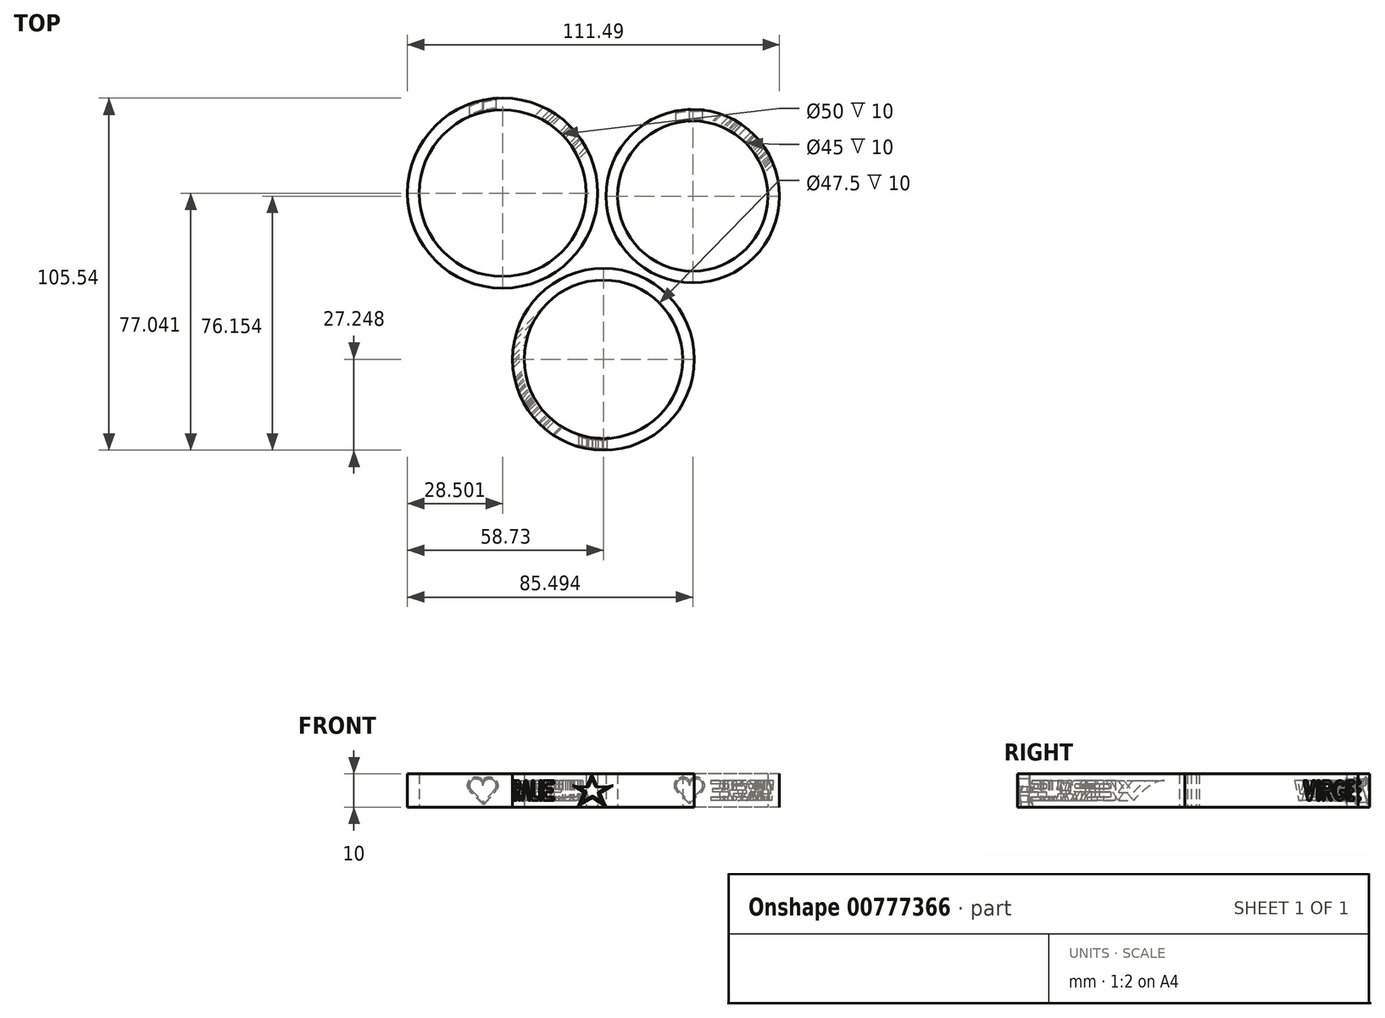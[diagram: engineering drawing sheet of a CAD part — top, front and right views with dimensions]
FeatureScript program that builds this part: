
annotation { "Feature Type Name" : "Feature", "Feature Type Description" : "" }
export const myFeature = defineFeature(function(context is Context, id is Id, definition is map)
    precondition{}
    {
        {
            var Q0;
            Q0=qCreatedBy(makeId("Top.planeOp"),FACE);
            var sketch = newSketch(context, id + "F0", { "sketchPlane" : qUnion([Q0])});
            skCircle(sketch, "E0", {"center": v(-30.23, 32.27) * mm, "radius": 25 * mm});
            skCircle(sketch, "E1", {"center": v(-30.23, 32.27) * mm, "radius": 28.5 * mm});
            skCircle(sketch, "E2", {"center": v(26.76, 31.38) * mm, "radius": 22.5 * mm});
            skCircle(sketch, "E3", {"center": v(26.76, 31.38) * mm, "radius": 26 * mm});
            skCircle(sketch, "E4", {"center": v(0, -17.52) * mm, "radius": 23.75 * mm});
            skCircle(sketch, "E5", {"center": v(0, -17.52) * mm, "radius": 27.25 * mm});
            skSolve(sketch);
        }
        {
            var Q0;
            Q0=makeQuery(id+"F0.imprint","IMPRINT",FACE,{"disambiguationData":[TD([[makeQuery(id+"F0.imprint","IMPRINT",EDGE,{"derivedFrom":sQuery(id+"F0.wireOp",EDGE,"E4")}),-1.0]])]});
            var Q1;
            Q1=makeQuery(id+"F0.imprint","IMPRINT",FACE,{"disambiguationData":[TD([[makeQuery(id+"F0.imprint","IMPRINT",EDGE,{"derivedFrom":sQuery(id+"F0.wireOp",EDGE,"E2")}),-1.0]])]});
            var Q2;
            Q2=makeQuery(id+"F0.imprint","IMPRINT",FACE,{"disambiguationData":[TD([[makeQuery(id+"F0.imprint","IMPRINT",EDGE,{"derivedFrom":sQuery(id+"F0.wireOp",EDGE,"E0")}),-1.0]])]});
            extrude(context, id + "F1", {"entities" : qUnion([Q0, Q1, Q2]), "depth" : 10 * mm, "offsetDistance" : 25 * mm});
        }
        {
            var Q0;
            Q0=qCreatedBy(makeId("Front.planeOp"),FACE);
            cPlane(context, id + "F2", {"entities" : qUnion([Q0]), "cplaneType" : CPlaneType.OFFSET, "offset" : 81.8 * mm, "width" : 150 * mm, "height" : 150 * mm});
        }
        {
            var Q0;
            Q0=qCreatedBy(id+"F2.planeOp",FACE);
            var sketch = newSketch(context, id + "F3", { "sketchPlane" : qUnion([Q0])});
            skLineSegment(sketch, "E6", {"start": v(-3.41, 8.5) * mm, "end": v(-0.41, 1.5) * mm});
            skLineSegment(sketch, "E7", {"start": v(-0.41, 1.5) * mm, "end": v(-7.41, 6) * mm});
            skLineSegment(sketch, "E8", {"start": v(-7.41, 6) * mm, "end": v(1.09, 6) * mm});
            skLineSegment(sketch, "E9", {"start": v(1.09, 6) * mm, "end": v(-6.41, 1.5) * mm});
            skLineSegment(sketch, "E10", {"start": v(-6.41, 1.5) * mm, "end": v(-3.41, 8.5) * mm});
            skSolve(sketch);
        }
        {
            var Q0;
            {var subQ0=sQuery(id+"F3.wireOp",EDGE,"E10");var subQ1=sQuery(id+"F3.wireOp",EDGE,"E6");var subQ2=makeQuery(id+"F3.imprint","INTERSECT",VERTEX,{"derivedFrom":[subQ1,subQ0]});Q0=makeQuery(id+"F3.imprint","IMPRINT",FACE,{"disambiguationData":[TD([[makeQuery(id+"F3.imprint","IMPRINT",EDGE,{"disambiguationData":[TD([[subQ2,-1.0]])],"derivedFrom":subQ1}),-1.0]])]});}
            var Q1;
            {var subQ0=sQuery(id+"F3.wireOp",EDGE,"E7");var subQ1=sQuery(id+"F3.wireOp",EDGE,"E6");var subQ2=makeQuery(id+"F3.imprint","INTERSECT",VERTEX,{"derivedFrom":[subQ1,subQ0]});Q1=makeQuery(id+"F3.imprint","IMPRINT",FACE,{"disambiguationData":[TD([[makeQuery(id+"F3.imprint","IMPRINT",EDGE,{"disambiguationData":[TD([[subQ2,1.0]])],"derivedFrom":subQ1}),-1.0]])]});}
            var Q2;
            {var subQ0=sQuery(id+"F3.wireOp",EDGE,"E9");var subQ1=sQuery(id+"F3.wireOp",EDGE,"E7");var subQ2=makeQuery(id+"F3.imprint","INTERSECT",VERTEX,{"derivedFrom":[subQ1,subQ0]});Q2=makeQuery(id+"F3.imprint","IMPRINT",FACE,{"disambiguationData":[TD([[makeQuery(id+"F3.imprint","IMPRINT",EDGE,{"disambiguationData":[TD([[subQ2,-1.0]])],"derivedFrom":subQ1}),1.0]])]});}
            var Q3;
            {var subQ1=sQuery(id+"F3.wireOp",EDGE,"E6");var subQ5=sQuery(id+"F3.wireOp",EDGE,"E8");var subQ6=makeQuery(id+"F3.imprint","INTERSECT",VERTEX,{"derivedFrom":[subQ1,subQ5]});Q3=makeQuery(id+"F3.imprint","IMPRINT",FACE,{"disambiguationData":[TD([[makeQuery(id+"F3.imprint","IMPRINT",EDGE,{"disambiguationData":[TD([[subQ6,-1.0]])],"derivedFrom":subQ1}),-1.0]])]});}
            var Q4;
            {var subQ0=sQuery(id+"F3.wireOp",EDGE,"E8");var subQ1=sQuery(id+"F3.wireOp",EDGE,"E6");var subQ2=makeQuery(id+"F3.imprint","INTERSECT",VERTEX,{"derivedFrom":[subQ1,subQ0]});Q4=makeQuery(id+"F3.imprint","IMPRINT",FACE,{"disambiguationData":[TD([[makeQuery(id+"F3.imprint","IMPRINT",EDGE,{"disambiguationData":[TD([[subQ2,-1.0]])],"derivedFrom":subQ1}),1.0]])]});}
            var Q5;
            {var subQ0=sQuery(id+"F3.wireOp",EDGE,"E8");var subQ1=sQuery(id+"F3.wireOp",EDGE,"E7");var subQ2=makeQuery(id+"F3.imprint","INTERSECT",VERTEX,{"derivedFrom":[subQ1,subQ0]});Q5=makeQuery(id+"F3.imprint","IMPRINT",FACE,{"disambiguationData":[TD([[makeQuery(id+"F3.imprint","IMPRINT",EDGE,{"disambiguationData":[TD([[subQ2,1.0]])],"derivedFrom":subQ1}),-1.0]])]});}
            extrude(context, id + "F4", {"entities" : qUnion([Q0, Q1, Q2, Q3, Q4, Q5]), "operationType" : NewBodyOperationType.REMOVE, "oppositeDirection" : true, "depth" : 58.8 * mm, "offsetDistance" : 25 * mm});
        }
        {
            var Q0;
            {var subQ0=sQuery(id+"F3.wireOp",EDGE,"E7");Q0=makeQuery(id+"F4.boolean.opBoolean","INTERSECT",EDGE,{"derivedFrom":[makeQuery(id+"F1.opExtrude","SWEPT_FACE",FACE,{"disambiguationData":[OSD([sQuery(id+"F0.wireOp",EDGE,"E4")])]}),makeQuery(id+"F4.opExtrude","SWEPT_FACE",FACE,{"disambiguationData":[OSD([subQ0]),TDD([makeQuery(id+"F3.imprint","IMPRINT",EDGE,{"disambiguationData":[TD([[makeQuery(id+"F3.imprint","INTERSECT",VERTEX,{"derivedFrom":[sQuery(id+"F3.wireOp",EDGE,"E6"),subQ0]}),-1.0]])],"derivedFrom":subQ0})])]})]});}
            var Q1;
            {var subQ0=sQuery(id+"F3.wireOp",EDGE,"E6");Q1=makeQuery(id+"F4.boolean.opBoolean","INTERSECT",EDGE,{"derivedFrom":[makeQuery(id+"F1.opExtrude","SWEPT_FACE",FACE,{"disambiguationData":[OSD([sQuery(id+"F0.wireOp",EDGE,"E4")])]}),makeQuery(id+"F4.opExtrude","SWEPT_FACE",FACE,{"disambiguationData":[OSD([subQ0]),TDD([makeQuery(id+"F3.imprint","IMPRINT",EDGE,{"disambiguationData":[TD([[makeQuery(id+"F3.imprint","INTERSECT",VERTEX,{"derivedFrom":[subQ0,sQuery(id+"F3.wireOp",EDGE,"E7")]}),1.0]])],"derivedFrom":subQ0})])]})]});}
            var Q2;
            {var subQ0=sQuery(id+"F3.wireOp",EDGE,"E9");Q2=makeQuery(id+"F4.boolean.opBoolean","INTERSECT",EDGE,{"derivedFrom":[makeQuery(id+"F1.opExtrude","SWEPT_FACE",FACE,{"disambiguationData":[OSD([sQuery(id+"F0.wireOp",EDGE,"E4")])]}),makeQuery(id+"F4.opExtrude","SWEPT_FACE",FACE,{"disambiguationData":[OSD([subQ0]),TDD([makeQuery(id+"F3.imprint","IMPRINT",EDGE,{"disambiguationData":[TD([[makeQuery(id+"F3.imprint","INTERSECT",VERTEX,{"derivedFrom":[sQuery(id+"F3.wireOp",EDGE,"E8"),subQ0]}),-1.0]])],"derivedFrom":subQ0})])]})]});}
            var Q3;
            {var subQ0=sQuery(id+"F3.wireOp",EDGE,"E8");Q3=makeQuery(id+"F4.boolean.opBoolean","INTERSECT",EDGE,{"derivedFrom":[makeQuery(id+"F1.opExtrude","SWEPT_FACE",FACE,{"disambiguationData":[OSD([sQuery(id+"F0.wireOp",EDGE,"E4")])]}),makeQuery(id+"F4.opExtrude","SWEPT_FACE",FACE,{"disambiguationData":[OSD([subQ0]),TDD([makeQuery(id+"F3.imprint","IMPRINT",EDGE,{"disambiguationData":[TD([[makeQuery(id+"F3.imprint","INTERSECT",VERTEX,{"derivedFrom":[subQ0,sQuery(id+"F3.wireOp",EDGE,"E9")]}),1.0]])],"derivedFrom":subQ0})])]})]});}
            var Q4;
            {var subQ0=sQuery(id+"F3.wireOp",EDGE,"E6");Q4=makeQuery(id+"F4.boolean.opBoolean","INTERSECT",EDGE,{"derivedFrom":[makeQuery(id+"F1.opExtrude","SWEPT_FACE",FACE,{"disambiguationData":[OSD([sQuery(id+"F0.wireOp",EDGE,"E4")])]}),makeQuery(id+"F4.opExtrude","SWEPT_FACE",FACE,{"disambiguationData":[OSD([subQ0]),TDD([makeQuery(id+"F3.imprint","IMPRINT",EDGE,{"disambiguationData":[TD([[makeQuery(id+"F3.imprint","INTERSECT",VERTEX,{"derivedFrom":[subQ0,sQuery(id+"F3.wireOp",EDGE,"E10")]}),-1.0]])],"derivedFrom":subQ0})])]})]});}
            var Q5;
            {var subQ0=sQuery(id+"F3.wireOp",EDGE,"E10");Q5=makeQuery(id+"F4.boolean.opBoolean","INTERSECT",EDGE,{"derivedFrom":[makeQuery(id+"F1.opExtrude","SWEPT_FACE",FACE,{"disambiguationData":[OSD([sQuery(id+"F0.wireOp",EDGE,"E4")])]}),makeQuery(id+"F4.opExtrude","SWEPT_FACE",FACE,{"disambiguationData":[OSD([subQ0]),TDD([makeQuery(id+"F3.imprint","IMPRINT",EDGE,{"disambiguationData":[TD([[makeQuery(id+"F3.imprint","INTERSECT",VERTEX,{"derivedFrom":[sQuery(id+"F3.wireOp",EDGE,"E6"),subQ0]}),1.0]])],"derivedFrom":subQ0})])]})]});}
            var Q6;
            {var subQ0=sQuery(id+"F3.wireOp",EDGE,"E8");Q6=makeQuery(id+"F4.boolean.opBoolean","INTERSECT",EDGE,{"derivedFrom":[makeQuery(id+"F1.opExtrude","SWEPT_FACE",FACE,{"disambiguationData":[OSD([sQuery(id+"F0.wireOp",EDGE,"E4")])]}),makeQuery(id+"F4.opExtrude","SWEPT_FACE",FACE,{"disambiguationData":[OSD([subQ0]),TDD([makeQuery(id+"F3.imprint","IMPRINT",EDGE,{"disambiguationData":[TD([[makeQuery(id+"F3.imprint","INTERSECT",VERTEX,{"derivedFrom":[sQuery(id+"F3.wireOp",EDGE,"E7"),subQ0]}),-1.0]])],"derivedFrom":subQ0})])]})]});}
            var Q7;
            {var subQ0=sQuery(id+"F3.wireOp",EDGE,"E7");Q7=makeQuery(id+"F4.boolean.opBoolean","INTERSECT",EDGE,{"derivedFrom":[makeQuery(id+"F1.opExtrude","SWEPT_FACE",FACE,{"disambiguationData":[OSD([sQuery(id+"F0.wireOp",EDGE,"E4")])]}),makeQuery(id+"F4.opExtrude","SWEPT_FACE",FACE,{"disambiguationData":[OSD([subQ0]),TDD([makeQuery(id+"F3.imprint","IMPRINT",EDGE,{"disambiguationData":[TD([[makeQuery(id+"F3.imprint","INTERSECT",VERTEX,{"derivedFrom":[subQ0,sQuery(id+"F3.wireOp",EDGE,"E8")]}),1.0]])],"derivedFrom":subQ0})])]})]});}
            var Q8;
            {var subQ0=sQuery(id+"F3.wireOp",EDGE,"E10");Q8=makeQuery(id+"F4.boolean.opBoolean","INTERSECT",EDGE,{"derivedFrom":[makeQuery(id+"F1.opExtrude","SWEPT_FACE",FACE,{"disambiguationData":[OSD([sQuery(id+"F0.wireOp",EDGE,"E4")])]}),makeQuery(id+"F4.opExtrude","SWEPT_FACE",FACE,{"disambiguationData":[OSD([subQ0]),TDD([makeQuery(id+"F3.imprint","IMPRINT",EDGE,{"disambiguationData":[TD([[makeQuery(id+"F3.imprint","INTERSECT",VERTEX,{"derivedFrom":[sQuery(id+"F3.wireOp",EDGE,"E9"),subQ0]}),-1.0]])],"derivedFrom":subQ0})])]})]});}
            var Q9;
            {var subQ0=sQuery(id+"F3.wireOp",EDGE,"E9");Q9=makeQuery(id+"F4.boolean.opBoolean","INTERSECT",EDGE,{"derivedFrom":[makeQuery(id+"F1.opExtrude","SWEPT_FACE",FACE,{"disambiguationData":[OSD([sQuery(id+"F0.wireOp",EDGE,"E4")])]}),makeQuery(id+"F4.opExtrude","SWEPT_FACE",FACE,{"disambiguationData":[OSD([subQ0]),TDD([makeQuery(id+"F3.imprint","IMPRINT",EDGE,{"disambiguationData":[TD([[makeQuery(id+"F3.imprint","INTERSECT",VERTEX,{"derivedFrom":[subQ0,sQuery(id+"F3.wireOp",EDGE,"E10")]}),1.0]])],"derivedFrom":subQ0})])]})]});}
            fillet(context, id + "F5", {"entities" : qUnion([Q0, Q1, Q2, Q3, Q4, Q5, Q6, Q7, Q8, Q9]), "radius" : .5 * mm, "tangentPropagation" : true, "allowEdgeOverflow" : false});
        }
        {
            var Q0;
            {var subQ0=sQuery(id+"F3.wireOp",EDGE,"E7");Q0=makeQuery(id+"F4.boolean.opBoolean","INTERSECT",EDGE,{"derivedFrom":[makeQuery(id+"F1.opExtrude","SWEPT_FACE",FACE,{"disambiguationData":[OSD([sQuery(id+"F0.wireOp",EDGE,"E5")])]}),makeQuery(id+"F4.opExtrude","SWEPT_FACE",FACE,{"disambiguationData":[OSD([subQ0]),TDD([makeQuery(id+"F3.imprint","IMPRINT",EDGE,{"disambiguationData":[TD([[makeQuery(id+"F3.imprint","INTERSECT",VERTEX,{"derivedFrom":[sQuery(id+"F3.wireOp",EDGE,"E6"),subQ0]}),-1.0]])],"derivedFrom":subQ0})])]})]});}
            var Q1;
            {var subQ0=sQuery(id+"F3.wireOp",EDGE,"E9");Q1=makeQuery(id+"F4.boolean.opBoolean","INTERSECT",EDGE,{"derivedFrom":[makeQuery(id+"F1.opExtrude","SWEPT_FACE",FACE,{"disambiguationData":[OSD([sQuery(id+"F0.wireOp",EDGE,"E5")])]}),makeQuery(id+"F4.opExtrude","SWEPT_FACE",FACE,{"disambiguationData":[OSD([subQ0]),TDD([makeQuery(id+"F3.imprint","IMPRINT",EDGE,{"disambiguationData":[TD([[makeQuery(id+"F3.imprint","INTERSECT",VERTEX,{"derivedFrom":[subQ0,sQuery(id+"F3.wireOp",EDGE,"E10")]}),1.0]])],"derivedFrom":subQ0})])]})]});}
            var Q2;
            {var subQ0=sQuery(id+"F3.wireOp",EDGE,"E10");Q2=makeQuery(id+"F4.boolean.opBoolean","INTERSECT",EDGE,{"derivedFrom":[makeQuery(id+"F1.opExtrude","SWEPT_FACE",FACE,{"disambiguationData":[OSD([sQuery(id+"F0.wireOp",EDGE,"E5")])]}),makeQuery(id+"F4.opExtrude","SWEPT_FACE",FACE,{"disambiguationData":[OSD([subQ0]),TDD([makeQuery(id+"F3.imprint","IMPRINT",EDGE,{"disambiguationData":[TD([[makeQuery(id+"F3.imprint","INTERSECT",VERTEX,{"derivedFrom":[sQuery(id+"F3.wireOp",EDGE,"E9"),subQ0]}),-1.0]])],"derivedFrom":subQ0})])]})]});}
            var Q3;
            {var subQ0=sQuery(id+"F3.wireOp",EDGE,"E7");Q3=makeQuery(id+"F4.boolean.opBoolean","INTERSECT",EDGE,{"derivedFrom":[makeQuery(id+"F1.opExtrude","SWEPT_FACE",FACE,{"disambiguationData":[OSD([sQuery(id+"F0.wireOp",EDGE,"E5")])]}),makeQuery(id+"F4.opExtrude","SWEPT_FACE",FACE,{"disambiguationData":[OSD([subQ0]),TDD([makeQuery(id+"F3.imprint","IMPRINT",EDGE,{"disambiguationData":[TD([[makeQuery(id+"F3.imprint","INTERSECT",VERTEX,{"derivedFrom":[subQ0,sQuery(id+"F3.wireOp",EDGE,"E8")]}),1.0]])],"derivedFrom":subQ0})])]})]});}
            var Q4;
            {var subQ0=sQuery(id+"F3.wireOp",EDGE,"E8");Q4=makeQuery(id+"F4.boolean.opBoolean","INTERSECT",EDGE,{"derivedFrom":[makeQuery(id+"F1.opExtrude","SWEPT_FACE",FACE,{"disambiguationData":[OSD([sQuery(id+"F0.wireOp",EDGE,"E5")])]}),makeQuery(id+"F4.opExtrude","SWEPT_FACE",FACE,{"disambiguationData":[OSD([subQ0]),TDD([makeQuery(id+"F3.imprint","IMPRINT",EDGE,{"disambiguationData":[TD([[makeQuery(id+"F3.imprint","INTERSECT",VERTEX,{"derivedFrom":[sQuery(id+"F3.wireOp",EDGE,"E7"),subQ0]}),-1.0]])],"derivedFrom":subQ0})])]})]});}
            var Q5;
            {var subQ0=sQuery(id+"F3.wireOp",EDGE,"E10");Q5=makeQuery(id+"F4.boolean.opBoolean","INTERSECT",EDGE,{"derivedFrom":[makeQuery(id+"F1.opExtrude","SWEPT_FACE",FACE,{"disambiguationData":[OSD([sQuery(id+"F0.wireOp",EDGE,"E5")])]}),makeQuery(id+"F4.opExtrude","SWEPT_FACE",FACE,{"disambiguationData":[OSD([subQ0]),TDD([makeQuery(id+"F3.imprint","IMPRINT",EDGE,{"disambiguationData":[TD([[makeQuery(id+"F3.imprint","INTERSECT",VERTEX,{"derivedFrom":[sQuery(id+"F3.wireOp",EDGE,"E6"),subQ0]}),1.0]])],"derivedFrom":subQ0})])]})]});}
            var Q6;
            {var subQ0=sQuery(id+"F3.wireOp",EDGE,"E6");Q6=makeQuery(id+"F4.boolean.opBoolean","INTERSECT",EDGE,{"derivedFrom":[makeQuery(id+"F1.opExtrude","SWEPT_FACE",FACE,{"disambiguationData":[OSD([sQuery(id+"F0.wireOp",EDGE,"E5")])]}),makeQuery(id+"F4.opExtrude","SWEPT_FACE",FACE,{"disambiguationData":[OSD([subQ0]),TDD([makeQuery(id+"F3.imprint","IMPRINT",EDGE,{"disambiguationData":[TD([[makeQuery(id+"F3.imprint","INTERSECT",VERTEX,{"derivedFrom":[subQ0,sQuery(id+"F3.wireOp",EDGE,"E10")]}),-1.0]])],"derivedFrom":subQ0})])]})]});}
            var Q7;
            {var subQ0=sQuery(id+"F3.wireOp",EDGE,"E8");Q7=makeQuery(id+"F4.boolean.opBoolean","INTERSECT",EDGE,{"derivedFrom":[makeQuery(id+"F1.opExtrude","SWEPT_FACE",FACE,{"disambiguationData":[OSD([sQuery(id+"F0.wireOp",EDGE,"E5")])]}),makeQuery(id+"F4.opExtrude","SWEPT_FACE",FACE,{"disambiguationData":[OSD([subQ0]),TDD([makeQuery(id+"F3.imprint","IMPRINT",EDGE,{"disambiguationData":[TD([[makeQuery(id+"F3.imprint","INTERSECT",VERTEX,{"derivedFrom":[subQ0,sQuery(id+"F3.wireOp",EDGE,"E9")]}),1.0]])],"derivedFrom":subQ0})])]})]});}
            var Q8;
            {var subQ0=sQuery(id+"F3.wireOp",EDGE,"E9");Q8=makeQuery(id+"F4.boolean.opBoolean","INTERSECT",EDGE,{"derivedFrom":[makeQuery(id+"F1.opExtrude","SWEPT_FACE",FACE,{"disambiguationData":[OSD([sQuery(id+"F0.wireOp",EDGE,"E5")])]}),makeQuery(id+"F4.opExtrude","SWEPT_FACE",FACE,{"disambiguationData":[OSD([subQ0]),TDD([makeQuery(id+"F3.imprint","IMPRINT",EDGE,{"disambiguationData":[TD([[makeQuery(id+"F3.imprint","INTERSECT",VERTEX,{"derivedFrom":[sQuery(id+"F3.wireOp",EDGE,"E8"),subQ0]}),-1.0]])],"derivedFrom":subQ0})])]})]});}
            var Q9;
            {var subQ0=sQuery(id+"F3.wireOp",EDGE,"E6");Q9=makeQuery(id+"F4.boolean.opBoolean","INTERSECT",EDGE,{"derivedFrom":[makeQuery(id+"F1.opExtrude","SWEPT_FACE",FACE,{"disambiguationData":[OSD([sQuery(id+"F0.wireOp",EDGE,"E5")])]}),makeQuery(id+"F4.opExtrude","SWEPT_FACE",FACE,{"disambiguationData":[OSD([subQ0]),TDD([makeQuery(id+"F3.imprint","IMPRINT",EDGE,{"disambiguationData":[TD([[makeQuery(id+"F3.imprint","INTERSECT",VERTEX,{"derivedFrom":[subQ0,sQuery(id+"F3.wireOp",EDGE,"E7")]}),1.0]])],"derivedFrom":subQ0})])]})]});}
            fillet(context, id + "F6", {"entities" : qUnion([Q0, Q1, Q2, Q3, Q4, Q5, Q6, Q7, Q8, Q9]), "radius" : .5 * mm, "tangentPropagation" : true, "allowEdgeOverflow" : false});
        }
        {
            var Q0;
            Q0=qCreatedBy(makeId("Front.planeOp"),FACE);
            cPlane(context, id + "F7", {"entities" : qUnion([Q0]), "cplaneType" : CPlaneType.OFFSET, "offset" : 109.91 * mm, "oppositeDirection" : true, "width" : 150 * mm, "height" : 150 * mm});
        }
        {
            var Q0;
            Q0=qCreatedBy(id+"F7.planeOp",FACE);
            var sketch = newSketch(context, id + "F8", { "sketchPlane" : qUnion([Q0])});
            skArc(sketch, "E11", {"start": v(-32.64, 5.17) * mm, "mid": v(-33.43, 8.37) * mm, "end": v(-36.14, 6.5) * mm});
            skArc(sketch, "E12", {"start": v(-36.14, 6.5) * mm, "mid": v(-38.91, 8.34) * mm, "end": v(-39.54, 5.07) * mm});
            skLineSegment(sketch, "E13", {"start": v(-35.9, 1.5) * mm, "end": v(-39.54, 5.07) * mm});
            skLineSegment(sketch, "E14", {"start": v(-39.54, 5.07) * mm, "end": v(-35.9, 1.5) * mm});
            skLineSegment(sketch, "E15", {"start": v(-35.9, 1.5) * mm, "end": v(-32.64, 5.17) * mm});
            skPoint(sketch, "E16.orphan", {"position": v(-35.9, -6.56) * mm});
            skSolve(sketch);
        }
        {
            var Q0;
            Q0 = qSketchRegion(id + "F8", true);
            extrude(context, id + "F9", {"entities" : qUnion([Q0]), "operationType" : NewBodyOperationType.REMOVE, "depth" : 65 * mm, "offsetDistance" : 25 * mm});
        }
        {
            var Q0;
            Q0=makeQuery(id+"F9.boolean.opBoolean","INTERSECT",EDGE,{"derivedFrom":[makeQuery(id+"F1.opExtrude","SWEPT_FACE",FACE,{"disambiguationData":[OSD([sQuery(id+"F0.wireOp",EDGE,"E0")])]}),makeQuery(id+"F9.opExtrude","SWEPT_FACE",FACE,{"disambiguationData":[OSD([sQuery(id+"F8.wireOp",EDGE,"E15")])]})]});
            var Q1;
            Q1=makeQuery(id+"F9.boolean.opBoolean","INTERSECT",EDGE,{"derivedFrom":[makeQuery(id+"F1.opExtrude","SWEPT_FACE",FACE,{"disambiguationData":[OSD([sQuery(id+"F0.wireOp",EDGE,"E0")])]}),makeQuery(id+"F9.opExtrude","SWEPT_FACE",FACE,{"disambiguationData":[OSD([sQuery(id+"F8.wireOp",EDGE,"E14")])]})]});
            var Q2;
            Q2=makeQuery(id+"F9.boolean.opBoolean","INTERSECT",EDGE,{"derivedFrom":[makeQuery(id+"F1.opExtrude","SWEPT_FACE",FACE,{"disambiguationData":[OSD([sQuery(id+"F0.wireOp",EDGE,"E0")])]}),makeQuery(id+"F9.opExtrude","SWEPT_FACE",FACE,{"disambiguationData":[OSD([sQuery(id+"F8.wireOp",EDGE,"E12")])]})]});
            var Q3;
            Q3=makeQuery(id+"F9.boolean.opBoolean","INTERSECT",EDGE,{"derivedFrom":[makeQuery(id+"F1.opExtrude","SWEPT_FACE",FACE,{"disambiguationData":[OSD([sQuery(id+"F0.wireOp",EDGE,"E0")])]}),makeQuery(id+"F9.opExtrude","SWEPT_FACE",FACE,{"disambiguationData":[OSD([sQuery(id+"F8.wireOp",EDGE,"E11")])]})]});
            fillet(context, id + "F10", {"entities" : qUnion([Q0, Q1, Q2, Q3]), "radius" : .5 * mm, "tangentPropagation" : true, "allowEdgeOverflow" : false});
        }
        {
            var Q0;
            Q0=makeQuery(id+"F9.boolean.opBoolean","INTERSECT",EDGE,{"derivedFrom":[makeQuery(id+"F1.opExtrude","SWEPT_FACE",FACE,{"disambiguationData":[OSD([sQuery(id+"F0.wireOp",EDGE,"E1")])]}),makeQuery(id+"F9.opExtrude","SWEPT_FACE",FACE,{"disambiguationData":[OSD([sQuery(id+"F8.wireOp",EDGE,"E14")])]})]});
            var Q1;
            Q1=makeQuery(id+"F9.boolean.opBoolean","INTERSECT",EDGE,{"derivedFrom":[makeQuery(id+"F1.opExtrude","SWEPT_FACE",FACE,{"disambiguationData":[OSD([sQuery(id+"F0.wireOp",EDGE,"E1")])]}),makeQuery(id+"F9.opExtrude","SWEPT_FACE",FACE,{"disambiguationData":[OSD([sQuery(id+"F8.wireOp",EDGE,"E15")])]})]});
            var Q2;
            Q2=makeQuery(id+"F9.boolean.opBoolean","INTERSECT",EDGE,{"derivedFrom":[makeQuery(id+"F1.opExtrude","SWEPT_FACE",FACE,{"disambiguationData":[OSD([sQuery(id+"F0.wireOp",EDGE,"E1")])]}),makeQuery(id+"F9.opExtrude","SWEPT_FACE",FACE,{"disambiguationData":[OSD([sQuery(id+"F8.wireOp",EDGE,"E12")])]})]});
            var Q3;
            Q3=makeQuery(id+"F9.boolean.opBoolean","INTERSECT",EDGE,{"derivedFrom":[makeQuery(id+"F1.opExtrude","SWEPT_FACE",FACE,{"disambiguationData":[OSD([sQuery(id+"F0.wireOp",EDGE,"E1")])]}),makeQuery(id+"F9.opExtrude","SWEPT_FACE",FACE,{"disambiguationData":[OSD([sQuery(id+"F8.wireOp",EDGE,"E11")])]})]});
            fillet(context, id + "F11", {"entities" : qUnion([Q0, Q1, Q2, Q3]), "radius" : .5 * mm, "tangentPropagation" : true, "allowEdgeOverflow" : false});
        }
        {
            var Q0;
            Q0=qCreatedBy(id+"F7.planeOp",FACE);
            var sketch = newSketch(context, id + "F12", { "sketchPlane" : qUnion([Q0])});
            skArc(sketch, "E17", {"start": v(29.18, 5.07) * mm, "mid": v(28.55, 8.34) * mm, "end": v(25.78, 6.5) * mm});
            skArc(sketch, "E18", {"start": v(25.78, 6.5) * mm, "mid": v(23, 8.34) * mm, "end": v(22.38, 5.07) * mm});
            skLineSegment(sketch, "E19", {"start": v(25.78, 1.74) * mm, "end": v(22.38, 5.07) * mm});
            skLineSegment(sketch, "E20", {"start": v(22.38, 5.07) * mm, "end": v(25.78, 1.74) * mm});
            skLineSegment(sketch, "E21", {"start": v(25.78, 1.74) * mm, "end": v(29.18, 5.07) * mm});
            skPoint(sketch, "E22.orphan", {"position": v(25.78, -4.26) * mm});
            skSolve(sketch);
        }
        {
            var Q0;
            Q0=makeQuery(id+"F12.imprint","IMPRINT",FACE,{"disambiguationData":[TD([[makeQuery(id+"F12.imprint","IMPRINT",EDGE,{"derivedFrom":sQuery(id+"F12.wireOp",EDGE,"E17")}),1.0]])]});
            extrude(context, id + "F13", {"entities" : qUnion([Q0]), "operationType" : NewBodyOperationType.REMOVE, "depth" : 92.4 * mm, "offsetDistance" : 25 * mm});
        }
        {
            var Q0;
            Q0=makeQuery(id+"F13.boolean.opBoolean","INTERSECT",EDGE,{"derivedFrom":[makeQuery(id+"F1.opExtrude","SWEPT_FACE",FACE,{"disambiguationData":[OSD([sQuery(id+"F0.wireOp",EDGE,"E2")])]}),makeQuery(id+"F13.opExtrude","SWEPT_FACE",FACE,{"disambiguationData":[OSD([sQuery(id+"F12.wireOp",EDGE,"E21")])]})]});
            var Q1;
            Q1=makeQuery(id+"F13.boolean.opBoolean","INTERSECT",EDGE,{"derivedFrom":[makeQuery(id+"F1.opExtrude","SWEPT_FACE",FACE,{"disambiguationData":[OSD([sQuery(id+"F0.wireOp",EDGE,"E2")])]}),makeQuery(id+"F13.opExtrude","SWEPT_FACE",FACE,{"disambiguationData":[OSD([sQuery(id+"F12.wireOp",EDGE,"E17")])]})]});
            var Q2;
            Q2=makeQuery(id+"F13.boolean.opBoolean","INTERSECT",EDGE,{"derivedFrom":[makeQuery(id+"F1.opExtrude","SWEPT_FACE",FACE,{"disambiguationData":[OSD([sQuery(id+"F0.wireOp",EDGE,"E2")])]}),makeQuery(id+"F13.opExtrude","SWEPT_FACE",FACE,{"disambiguationData":[OSD([sQuery(id+"F12.wireOp",EDGE,"E20")])]})]});
            var Q3;
            Q3=makeQuery(id+"F13.boolean.opBoolean","INTERSECT",EDGE,{"derivedFrom":[makeQuery(id+"F1.opExtrude","SWEPT_FACE",FACE,{"disambiguationData":[OSD([sQuery(id+"F0.wireOp",EDGE,"E2")])]}),makeQuery(id+"F13.opExtrude","SWEPT_FACE",FACE,{"disambiguationData":[OSD([sQuery(id+"F12.wireOp",EDGE,"E18")])]})]});
            fillet(context, id + "F14", {"entities" : qUnion([Q0, Q1, Q2, Q3]), "radius" : .5 * mm, "tangentPropagation" : true, "allowEdgeOverflow" : false});
        }
        {
            var Q0;
            Q0=makeQuery(id+"F13.boolean.opBoolean","INTERSECT",EDGE,{"derivedFrom":[makeQuery(id+"F1.opExtrude","SWEPT_FACE",FACE,{"disambiguationData":[OSD([sQuery(id+"F0.wireOp",EDGE,"E3")])]}),makeQuery(id+"F13.opExtrude","SWEPT_FACE",FACE,{"disambiguationData":[OSD([sQuery(id+"F12.wireOp",EDGE,"E20")])]})]});
            var Q1;
            Q1=makeQuery(id+"F13.boolean.opBoolean","INTERSECT",EDGE,{"derivedFrom":[makeQuery(id+"F1.opExtrude","SWEPT_FACE",FACE,{"disambiguationData":[OSD([sQuery(id+"F0.wireOp",EDGE,"E3")])]}),makeQuery(id+"F13.opExtrude","SWEPT_FACE",FACE,{"disambiguationData":[OSD([sQuery(id+"F12.wireOp",EDGE,"E18")])]})]});
            var Q2;
            Q2=makeQuery(id+"F13.boolean.opBoolean","INTERSECT",EDGE,{"derivedFrom":[makeQuery(id+"F1.opExtrude","SWEPT_FACE",FACE,{"disambiguationData":[OSD([sQuery(id+"F0.wireOp",EDGE,"E3")])]}),makeQuery(id+"F13.opExtrude","SWEPT_FACE",FACE,{"disambiguationData":[OSD([sQuery(id+"F12.wireOp",EDGE,"E17")])]})]});
            var Q3;
            Q3=makeQuery(id+"F13.boolean.opBoolean","INTERSECT",EDGE,{"derivedFrom":[makeQuery(id+"F1.opExtrude","SWEPT_FACE",FACE,{"disambiguationData":[OSD([sQuery(id+"F0.wireOp",EDGE,"E3")])]}),makeQuery(id+"F13.opExtrude","SWEPT_FACE",FACE,{"disambiguationData":[OSD([sQuery(id+"F12.wireOp",EDGE,"E21")])]})]});
            fillet(context, id + "F15", {"entities" : qUnion([Q0, Q1, Q2, Q3]), "radius" : .5 * mm, "tangentPropagation" : true, "allowEdgeOverflow" : false});
        }
        {
            var Q0;
            Q0=qCreatedBy(makeId("Right.planeOp"),FACE);
            var Q1;
            Q1=makeQuery(id+"F1.opExtrude","CAP_EDGE",EDGE,{"disambiguationData":[OSD([sQuery(id+"F0.wireOp",EDGE,"E5")])],"isStart":false});
            cPlane(context, id + "F16", {"entities" : qUnion([Q0, Q1]), "cplaneType" : CPlaneType.LINE_ANGLE, "offset" : 28.49 * mm, "angle" : 135 * degree, "oppositeDirection" : true, "width" : 150 * mm, "height" : 150 * mm});
        }
        {
            var Q0;
            Q0=qCreatedBy(id+"F16.planeOp",FACE);
            var sketch = newSketch(context, id + "F17", { "sketchPlane" : qUnion([Q0])});
            skLineSegment(sketch, "E23", {"start": v(11.37, 8) * mm, "end": v(8.87, 2) * mm});
            skLineSegment(sketch, "E24", {"start": v(8.87, 2) * mm, "end": v(8.87, 2) * mm});
            skLineSegment(sketch, "E25", {"start": v(8.87, 2) * mm, "end": v(6.37, 8) * mm});
            skLineSegment(sketch, "E26", {"start": v(6.37, 8) * mm, "end": v(7.37, 8) * mm});
            skLineSegment(sketch, "E27", {"start": v(7.37, 8) * mm, "end": v(8.87, 4.4) * mm});
            skLineSegment(sketch, "E28", {"start": v(8.87, 4.4) * mm, "end": v(10.37, 8) * mm});
            skLineSegment(sketch, "E29", {"start": v(10.37, 8) * mm, "end": v(11.37, 8) * mm});
            skPoint(sketch, "E30.orphan", {"position": v(6.37, 5) * mm});
            skLineSegment(sketch, "E31", {"start": v(1.37, 8) * mm, "end": v(1.37, 6.5) * mm});
            skLineSegment(sketch, "E32", {"start": v(1.37, 2) * mm, "end": v(0.37, 2) * mm});
            skLineSegment(sketch, "E33", {"start": v(0.37, 2) * mm, "end": v(0.37, 4.66) * mm});
            skPoint(sketch, "E34.end.orphan", {"position": v(-6.02, 5.66) * mm});
            skPoint(sketch, "E35.center.orphan", {"position": v(0.37, 6.56) * mm});
            skPoint(sketch, "E36.end.orphan", {"position": v(0.37, 8.36) * mm});
            skLineSegment(sketch, "E37.trimOffspring", {"start": v(0.37, 5.66) * mm, "end": v(0.37, 5.66) * mm});
            skPoint(sketch, "E38.center.orphan", {"position": v(0.37, 6.2) * mm});
            skLineSegment(sketch, "E39", {"start": v(0.37, 4.66) * mm, "end": v(-0.13, 4.66) * mm});
            skLineSegment(sketch, "E40", {"start": v(-0.13, 4.66) * mm, "end": v(-1.67, 2) * mm});
            skLineSegment(sketch, "E41", {"start": v(-1.67, 2) * mm, "end": v(-2.77, 2) * mm});
            skLineSegment(sketch, "E42", {"start": v(-2.77, 2) * mm, "end": v(-1.27, 4.6) * mm});
            skLineSegment(sketch, "E43", {"start": v(1.37, 8) * mm, "end": v(-1.13, 8) * mm});
            skArc(sketch, "E44", {"start": v(-1.13, 8) * mm, "mid": v(-2.83, 6.36) * mm, "end": v(-1.27, 4.6) * mm});
            skLineSegment(sketch, "E45", {"start": v(0.37, 7) * mm, "end": v(0.37, 6.5) * mm});
            skLineSegment(sketch, "E46", {"start": v(0.37, 7) * mm, "end": v(-1, 7) * mm});
            skLineSegment(sketch, "E47", {"start": v(0.37, 5.66) * mm, "end": v(-0.96, 5.66) * mm});
            skArc(sketch, "E48", {"start": v(-1, 7) * mm, "mid": v(-1.63, 6.3) * mm, "end": v(-0.96, 5.66) * mm});
            skLineSegment(sketch, "E49", {"start": v(0.37, 6.16) * mm, "end": v(1.37, 6.16) * mm});
            skLineSegment(sketch, "E50", {"start": v(0.37, 6.5) * mm, "end": v(1.37, 6.5) * mm});
            skLineSegment(sketch, "E51.trimOffspring", {"start": v(0.37, 6.16) * mm, "end": v(0.37, 5.66) * mm});
            skLineSegment(sketch, "E52.trimOffspring", {"start": v(1.37, 6.16) * mm, "end": v(1.37, 2) * mm});
            skLineSegment(sketch, "E53", {"start": v(-3.43, 2) * mm, "end": v(-5.36, 8) * mm});
            skLineSegment(sketch, "E54", {"start": v(-5.36, 8) * mm, "end": v(-6.66, 8) * mm});
            skLineSegment(sketch, "E55", {"start": v(-6.66, 8) * mm, "end": v(-8.6, 2) * mm});
            skLineSegment(sketch, "E56", {"start": v(-8.6, 2) * mm, "end": v(-7.54, 2) * mm});
            skLineSegment(sketch, "E57", {"start": v(-7.54, 2) * mm, "end": v(-6.9, 4) * mm});
            skLineSegment(sketch, "E58", {"start": v(-6.9, 4) * mm, "end": v(-6.26, 4) * mm});
            skLineSegment(sketch, "E59", {"start": v(-5.12, 4) * mm, "end": v(-4.48, 2) * mm});
            skLineSegment(sketch, "E60", {"start": v(-4.48, 2) * mm, "end": v(-3.43, 2) * mm});
            skLineSegment(sketch, "E61", {"start": v(-5.44, 5) * mm, "end": v(-6, 7.36) * mm});
            skLineSegment(sketch, "E62", {"start": v(-6, 7.36) * mm, "end": v(-6.57, 5) * mm});
            skLineSegment(sketch, "E63", {"start": v(-6.57, 5) * mm, "end": v(-6.26, 5) * mm});
            skLineSegment(sketch, "E64", {"start": v(-6.26, 5) * mm, "end": v(-6.26, 4) * mm});
            skLineSegment(sketch, "E65", {"start": v(-6.26, 4) * mm, "end": v(-6.26, 5) * mm});
            skLineSegment(sketch, "E66", {"start": v(-5.76, 5) * mm, "end": v(-5.76, 4) * mm});
            skLineSegment(sketch, "E67.trimOffspring", {"start": v(-5.76, 5) * mm, "end": v(-5.44, 5) * mm});
            skLineSegment(sketch, "E68.trimOffspring", {"start": v(-5.76, 4) * mm, "end": v(-5.12, 4) * mm});
            skLineSegment(sketch, "E69.bottom", {"start": v(-9.1, 8) * mm, "end": v(-10.1, 8) * mm});
            skLineSegment(sketch, "E69.top", {"start": v(-9.1, 2) * mm, "end": v(-10.1, 2) * mm});
            skLineSegment(sketch, "E69.left", {"start": v(-9.1, 8) * mm, "end": v(-9.1, 2) * mm});
            skLineSegment(sketch, "E69.right", {"start": v(-10.1, 8) * mm, "end": v(-10.1, 3) * mm});
            skLineSegment(sketch, "E70.bottom", {"start": v(-10.1, 2) * mm, "end": v(-12.1, 2) * mm});
            skLineSegment(sketch, "E70.top", {"start": v(-10.1, 3) * mm, "end": v(-12.1, 3) * mm});
            skLineSegment(sketch, "E70.right", {"start": v(-12.1, 2) * mm, "end": v(-12.1, 3) * mm});
            skLineSegment(sketch, "E71.bottom", {"start": v(-12.6, 2) * mm, "end": v(-13.6, 2) * mm});
            skLineSegment(sketch, "E71.top", {"start": v(-12.6, 8) * mm, "end": v(-13.6, 8) * mm});
            skLineSegment(sketch, "E71.left", {"start": v(-12.6, 2) * mm, "end": v(-12.6, 8) * mm});
            skLineSegment(sketch, "E71.right", {"start": v(-13.6, 2) * mm, "end": v(-13.6, 8) * mm});
            skPoint(sketch, "E72.orphan", {"position": v(-14.1, 5) * mm});
            skPoint(sketch, "E73.start.orphan", {"position": v(11.37, 7.94) * mm});
            skPoint(sketch, "E74.orphan", {"position": v(0.37, 5) * mm});
            skPoint(sketch, "E75.trimOffspring.end.orphan", {"position": v(5.1, 6) * mm});
            skPoint(sketch, "E76.end.orphan", {"position": v(3.6, 6) * mm});
            skPoint(sketch, "E77.end.orphan", {"position": v(3.6, 5) * mm});
            skPoint(sketch, "E78.center.orphan", {"position": v(3.37, 5) * mm});
            skPoint(sketch, "E79.trimOffspring.end.orphan", {"position": v(-20.1, 5) * mm});
            skPoint(sketch, "E80.trimOffspring.end.orphan", {"position": v(-16.86, 6) * mm});
            skPoint(sketch, "E81.center.orphan", {"position": v(-17.1, 5) * mm});
            skPoint(sketch, "E82.end.orphan", {"position": v(-18.36, 6) * mm});
            skPoint(sketch, "E82.start.orphan", {"position": v(-18.36, 5) * mm});
            skLineSegment(sketch, "E83.bottom", {"start": v(5.87, 8) * mm, "end": v(4.87, 8) * mm});
            skLineSegment(sketch, "E83.top", {"start": v(5.87, 2) * mm, "end": v(4.87, 2) * mm});
            skLineSegment(sketch, "E83.left", {"start": v(5.87, 8) * mm, "end": v(5.87, 2) * mm});
            skLineSegment(sketch, "E83.right", {"start": v(4.87, 8) * mm, "end": v(4.87, 2) * mm});
            skLineSegment(sketch, "E84.bottom", {"start": v(4.87, 8) * mm, "end": v(1.87, 8) * mm});
            skLineSegment(sketch, "E84.top", {"start": v(4.87, 7) * mm, "end": v(1.87, 7) * mm});
            skLineSegment(sketch, "E84.left", {"start": v(4.87, 8) * mm, "end": v(4.87, 7) * mm});
            skLineSegment(sketch, "E84.right", {"start": v(1.87, 8) * mm, "end": v(1.87, 7) * mm});
            skLineSegment(sketch, "E85.bottom", {"start": v(4.87, 2) * mm, "end": v(1.87, 2) * mm});
            skLineSegment(sketch, "E85.top", {"start": v(4.87, 3) * mm, "end": v(1.87, 3) * mm});
            skLineSegment(sketch, "E85.left", {"start": v(4.87, 2) * mm, "end": v(4.87, 3) * mm});
            skLineSegment(sketch, "E85.right", {"start": v(1.87, 2) * mm, "end": v(1.87, 3) * mm});
            skLineSegment(sketch, "E86.bottom", {"start": v(4.87, 4.5) * mm, "end": v(2.37, 4.5) * mm});
            skLineSegment(sketch, "E86.top", {"start": v(4.87, 5.5) * mm, "end": v(2.37, 5.5) * mm});
            skLineSegment(sketch, "E86.left", {"start": v(4.87, 4.5) * mm, "end": v(4.87, 5.5) * mm});
            skLineSegment(sketch, "E86.right", {"start": v(2.37, 4.5) * mm, "end": v(2.37, 5.5) * mm});
            skPoint(sketch, "E87.orphan", {"position": v(-13.6, 5) * mm});
            skPoint(sketch, "E88.trimOffspring.end.orphan", {"position": v(-14.87, 6) * mm});
            skPoint(sketch, "E89.end.orphan", {"position": v(-16.37, 6) * mm});
            skPoint(sketch, "E90.end.orphan", {"position": v(-16.37, 5) * mm});
            skPoint(sketch, "E91.center.orphan", {"position": v(-16.6, 5) * mm});
            skLineSegment(sketch, "E92.bottom", {"start": v(-14.1, 8) * mm, "end": v(-15.1, 8) * mm});
            skLineSegment(sketch, "E92.top", {"start": v(-14.1, 2) * mm, "end": v(-15.1, 2) * mm});
            skLineSegment(sketch, "E92.left", {"start": v(-14.1, 8) * mm, "end": v(-14.1, 2) * mm});
            skLineSegment(sketch, "E92.right", {"start": v(-15.1, 8) * mm, "end": v(-15.1, 2) * mm});
            skLineSegment(sketch, "E93.bottom", {"start": v(-15.1, 8) * mm, "end": v(-18.1, 8) * mm});
            skLineSegment(sketch, "E93.top", {"start": v(-15.1, 7) * mm, "end": v(-18.1, 7) * mm});
            skLineSegment(sketch, "E93.left", {"start": v(-15.1, 8) * mm, "end": v(-15.1, 7) * mm});
            skLineSegment(sketch, "E93.right", {"start": v(-18.1, 8) * mm, "end": v(-18.1, 7) * mm});
            skLineSegment(sketch, "E94.bottom", {"start": v(-15.1, 2) * mm, "end": v(-18.1, 2) * mm});
            skLineSegment(sketch, "E94.top", {"start": v(-15.1, 3) * mm, "end": v(-18.1, 3) * mm});
            skLineSegment(sketch, "E94.left", {"start": v(-15.1, 2) * mm, "end": v(-15.1, 3) * mm});
            skLineSegment(sketch, "E94.right", {"start": v(-18.1, 2) * mm, "end": v(-18.1, 3) * mm});
            skLineSegment(sketch, "E95.bottom", {"start": v(-15.1, 4.5) * mm, "end": v(-17.6, 4.5) * mm});
            skLineSegment(sketch, "E95.top", {"start": v(-15.1, 5.5) * mm, "end": v(-17.6, 5.5) * mm});
            skLineSegment(sketch, "E95.left", {"start": v(-15.1, 4.5) * mm, "end": v(-15.1, 5.5) * mm});
            skLineSegment(sketch, "E95.right", {"start": v(-17.6, 4.5) * mm, "end": v(-17.6, 5.5) * mm});
            skSolve(sketch);
        }
        {
            var Q0;
            Q0 = qSketchRegion(id + "F17", true);
            extrude(context, id + "F18", {"entities" : qUnion([Q0]), "operationType" : NewBodyOperationType.REMOVE, "oppositeDirection" : true, "depth" : 38.4 * mm, "offsetDistance" : 25 * mm});
        }
        {
            var Q0;
            Q0=qCreatedBy(makeId("Right.planeOp"),FACE);
            var Q1;
            Q1=makeQuery(id+"F1.opExtrude","CAP_EDGE",EDGE,{"disambiguationData":[OSD([sQuery(id+"F0.wireOp",EDGE,"E0")])],"isStart":false});
            cPlane(context, id + "F19", {"entities" : qUnion([Q0, Q1]), "cplaneType" : CPlaneType.LINE_ANGLE, "offset" : 25 * mm, "angle" : 135 * degree, "oppositeDirection" : true, "width" : 150 * mm, "height" : 150 * mm});
        }
        {
            var Q0;
            Q0=qCreatedBy(id+"F19.planeOp",FACE);
            var sketch = newSketch(context, id + "F20", { "sketchPlane" : qUnion([Q0])});
            skArc(sketch, "E96", {"start": v(36.27, 3.9) * mm, "mid": v(37.17, 3) * mm, "end": v(38.08, 3.9) * mm});
            skArc(sketch, "E97", {"start": v(35.27, 3.9) * mm, "mid": v(37.17, 2) * mm, "end": v(39.08, 3.9) * mm});
            skLineSegment(sketch, "E98.top", {"start": v(39.08, 8) * mm, "end": v(38.08, 8) * mm});
            skLineSegment(sketch, "E98.left", {"start": v(39.08, 3.9) * mm, "end": v(39.08, 8) * mm});
            skLineSegment(sketch, "E98.right", {"start": v(38.08, 3.9) * mm, "end": v(38.08, 8) * mm});
            skLineSegment(sketch, "E99", {"start": v(36.27, 3.9) * mm, "end": v(35.27, 3.9) * mm});
            skPoint(sketch, "E100.end.orphan", {"position": v(36.27, 8) * mm});
            skPoint(sketch, "E101.end.orphan", {"position": v(35.27, 8) * mm});
            skLineSegment(sketch, "E102", {"start": v(39.58, 8) * mm, "end": v(39.58, 3.9) * mm});
            skLineSegment(sketch, "E103", {"start": v(39.58, 3.9) * mm, "end": v(39.58, 8) * mm});
            skLineSegment(sketch, "E104", {"start": v(39.58, 8) * mm, "end": v(40.58, 8) * mm});
            skLineSegment(sketch, "E105", {"start": v(40.58, 8) * mm, "end": v(40.58, 3.9) * mm});
            skLineSegment(sketch, "E106", {"start": v(42.58, 8) * mm, "end": v(42.58, 3.9) * mm});
            skLineSegment(sketch, "E107", {"start": v(42.58, 3.9) * mm, "end": v(42.58, 8) * mm});
            skLineSegment(sketch, "E108", {"start": v(42.58, 8) * mm, "end": v(43.58, 8) * mm});
            skLineSegment(sketch, "E109", {"start": v(43.58, 8) * mm, "end": v(43.58, 3.9) * mm});
            skArc(sketch, "E110", {"start": v(40.58, 3.9) * mm, "mid": v(41.58, 2.9) * mm, "end": v(42.58, 3.9) * mm});
            skArc(sketch, "E111", {"start": v(39.58, 3.9) * mm, "mid": v(41.58, 1.9) * mm, "end": v(43.58, 3.9) * mm});
            skLineSegment(sketch, "E112", {"start": v(44.08, 8) * mm, "end": v(44.08, 1.9) * mm});
            skLineSegment(sketch, "E113", {"start": v(44.08, 1.9) * mm, "end": v(48.08, 1.9) * mm});
            skLineSegment(sketch, "E114", {"start": v(48.08, 1.9) * mm, "end": v(48.08, 2.9) * mm});
            skLineSegment(sketch, "E115", {"start": v(48.08, 2.9) * mm, "end": v(45.08, 2.9) * mm});
            skLineSegment(sketch, "E116", {"start": v(45.08, 2.9) * mm, "end": v(45.08, 8) * mm});
            skLineSegment(sketch, "E117", {"start": v(45.08, 8) * mm, "end": v(44.08, 8) * mm});
            skLineSegment(sketch, "E118.bottom", {"start": v(48.75, 1.9) * mm, "end": v(49.75, 1.9) * mm});
            skLineSegment(sketch, "E118.top", {"start": v(48.75, 8) * mm, "end": v(49.75, 8) * mm});
            skLineSegment(sketch, "E118.left", {"start": v(48.75, 1.9) * mm, "end": v(48.75, 8) * mm});
            skLineSegment(sketch, "E118.right", {"start": v(49.75, 1.9) * mm, "end": v(49.75, 8) * mm});
            skLineSegment(sketch, "E119", {"start": v(50.75, 8) * mm, "end": v(50.75, 2) * mm});
            skLineSegment(sketch, "E120", {"start": v(50.75, 2) * mm, "end": v(53.75, 2) * mm});
            skLineSegment(sketch, "E121", {"start": v(53.75, 2) * mm, "end": v(53.75, 3) * mm});
            skLineSegment(sketch, "E122", {"start": v(53.75, 3) * mm, "end": v(51.75, 3) * mm});
            skLineSegment(sketch, "E123", {"start": v(51.75, 3) * mm, "end": v(51.75, 4.5) * mm});
            skLineSegment(sketch, "E124", {"start": v(51.75, 4.5) * mm, "end": v(53.75, 4.5) * mm});
            skLineSegment(sketch, "E125", {"start": v(53.75, 4.5) * mm, "end": v(53.75, 5.5) * mm});
            skLineSegment(sketch, "E126", {"start": v(53.75, 5.5) * mm, "end": v(51.75, 5.5) * mm});
            skLineSegment(sketch, "E127", {"start": v(51.75, 5.5) * mm, "end": v(51.75, 7) * mm});
            skLineSegment(sketch, "E128", {"start": v(51.75, 7) * mm, "end": v(53.75, 7) * mm});
            skLineSegment(sketch, "E129", {"start": v(53.75, 7) * mm, "end": v(53.75, 8) * mm});
            skLineSegment(sketch, "E130", {"start": v(53.75, 8) * mm, "end": v(50.75, 8) * mm});
            skSolve(sketch);
        }
        {
            var Q0;
            Q0 = qSketchRegion(id + "F20", true);
            extrude(context, id + "F21", {"entities" : qUnion([Q0]), "operationType" : NewBodyOperationType.REMOVE, "depth" : 64.4 * mm, "offsetDistance" : 25 * mm});
        }
        {
            var Q0;
            Q0=qCreatedBy(makeId("Front.planeOp"),FACE);
            var Q1;
            Q1=makeQuery(id+"F1.opExtrude","CAP_EDGE",EDGE,{"disambiguationData":[OSD([sQuery(id+"F0.wireOp",EDGE,"E2")])],"isStart":false});
            cPlane(context, id + "F22", {"entities" : qUnion([Q0, Q1]), "cplaneType" : CPlaneType.LINE_ANGLE, "offset" : 25 * mm, "angle" : 135 * degree, "width" : 150 * mm, "height" : 150 * mm});
        }
        {
            var Q0;
            Q0=qCreatedBy(id+"F22.planeOp",FACE);
            var sketch = newSketch(context, id + "F23", { "sketchPlane" : qUnion([Q0])});
            skLineSegment(sketch, "E131", {"start": v(6.98, 8) * mm, "end": v(5.77, 2) * mm});
            skLineSegment(sketch, "E132", {"start": v(5.77, 2) * mm, "end": v(4.77, 2) * mm});
            skLineSegment(sketch, "E133", {"start": v(4.77, 2) * mm, "end": v(3.23, 8) * mm});
            skLineSegment(sketch, "E134", {"start": v(3.23, 8) * mm, "end": v(4.23, 8) * mm});
            skLineSegment(sketch, "E135", {"start": v(4.23, 8) * mm, "end": v(5.27, 3.95) * mm});
            skLineSegment(sketch, "E136", {"start": v(5.27, 3.95) * mm, "end": v(5.98, 8) * mm});
            skLineSegment(sketch, "E137", {"start": v(5.98, 8) * mm, "end": v(6.98, 8) * mm});
            skLineSegment(sketch, "E138.bottom", {"start": v(2.73, 8) * mm, "end": v(1.73, 8) * mm});
            skLineSegment(sketch, "E138.top", {"start": v(2.73, 2) * mm, "end": v(1.73, 2) * mm});
            skLineSegment(sketch, "E138.left", {"start": v(2.73, 8) * mm, "end": v(2.73, 2) * mm});
            skLineSegment(sketch, "E138.right", {"start": v(1.73, 8) * mm, "end": v(1.73, 2) * mm});
            skLineSegment(sketch, "E139", {"start": v(0.84, 8) * mm, "end": v(0.84, 6.5) * mm});
            skLineSegment(sketch, "E140", {"start": v(0.84, 8) * mm, "end": v(-1.33, 8) * mm});
            skLineSegment(sketch, "E141", {"start": v(0.84, 2) * mm, "end": v(-0.02, 2) * mm});
            skLineSegment(sketch, "E142", {"start": v(-0.02, 2) * mm, "end": v(-0.02, 4.5) * mm});
            skLineSegment(sketch, "E143", {"start": v(-0.02, 4.5) * mm, "end": v(-0.55, 4.5) * mm});
            skLineSegment(sketch, "E144", {"start": v(-0.55, 4.5) * mm, "end": v(-2.08, 2) * mm});
            skLineSegment(sketch, "E145", {"start": v(-2.08, 2) * mm, "end": v(-2.86, 2) * mm});
            skLineSegment(sketch, "E146", {"start": v(-2.86, 2) * mm, "end": v(-1.33, 4.5) * mm});
            skArc(sketch, "E147", {"start": v(-1.33, 8) * mm, "mid": v(-3.08, 6.25) * mm, "end": v(-1.33, 4.5) * mm});
            skLineSegment(sketch, "E148", {"start": v(-0.02, 7) * mm, "end": v(-0.02, 6.5) * mm});
            skLineSegment(sketch, "E149", {"start": v(-0.02, 5.5) * mm, "end": v(-0.02, 6) * mm});
            skLineSegment(sketch, "E150", {"start": v(-0.02, 7) * mm, "end": v(-1.33, 7) * mm});
            skLineSegment(sketch, "E151", {"start": v(-0.02, 5.5) * mm, "end": v(-1.33, 5.5) * mm});
            skArc(sketch, "E152", {"start": v(-1.33, 7) * mm, "mid": v(-2.08, 6.25) * mm, "end": v(-1.33, 5.5) * mm});
            skArc(sketch, "E153", {"start": v(-9.43, 5) * mm, "mid": v(-3.59, 4.04) * mm, "end": v(-8.8, 6.83) * mm});
            skArc(sketch, "E154", {"start": v(-8.16, 4) * mm, "mid": v(-4.44, 4.8) * mm, "end": v(-7.93, 6.32) * mm});
            skLineSegment(sketch, "E155", {"start": v(-9.43, 5) * mm, "end": v(-8.43, 5) * mm});
            skLineSegment(sketch, "E156", {"start": v(-8.8, 6.83) * mm, "end": v(-7.93, 6.32) * mm});
            skLineSegment(sketch, "E157", {"start": v(-6.43, 5) * mm, "end": v(-8.43, 5) * mm});
            skLineSegment(sketch, "E158", {"start": v(-6.43, 5) * mm, "end": v(-6.43, 4) * mm});
            skLineSegment(sketch, "E159", {"start": v(-6.43, 4) * mm, "end": v(-8.16, 4) * mm});
            skLineSegment(sketch, "E160.bottom", {"start": v(-9.93, 8) * mm, "end": v(-10.93, 8) * mm});
            skLineSegment(sketch, "E160.top", {"start": v(-9.93, 2) * mm, "end": v(-10.93, 2) * mm});
            skLineSegment(sketch, "E160.left", {"start": v(-9.93, 8) * mm, "end": v(-9.93, 2) * mm});
            skLineSegment(sketch, "E160.right", {"start": v(-10.93, 8) * mm, "end": v(-10.93, 2) * mm});
            skLineSegment(sketch, "E161", {"start": v(-11.43, 8) * mm, "end": v(-11.43, 2) * mm});
            skLineSegment(sketch, "E162", {"start": v(-11.43, 2) * mm, "end": v(-14.93, 2) * mm});
            skLineSegment(sketch, "E163", {"start": v(-14.93, 2) * mm, "end": v(-14.93, 3) * mm});
            skLineSegment(sketch, "E164", {"start": v(-14.93, 3) * mm, "end": v(-12.43, 3) * mm});
            skLineSegment(sketch, "E165", {"start": v(-12.43, 3) * mm, "end": v(-12.43, 4.5) * mm});
            skLineSegment(sketch, "E166", {"start": v(-12.43, 4.5) * mm, "end": v(-14.43, 4.5) * mm});
            skLineSegment(sketch, "E167", {"start": v(-14.43, 4.5) * mm, "end": v(-14.43, 5.5) * mm});
            skLineSegment(sketch, "E168", {"start": v(-14.43, 5.5) * mm, "end": v(-12.43, 5.5) * mm});
            skLineSegment(sketch, "E169", {"start": v(-12.43, 5.5) * mm, "end": v(-12.43, 7) * mm});
            skLineSegment(sketch, "E170", {"start": v(-12.43, 7) * mm, "end": v(-14.93, 7) * mm});
            skLineSegment(sketch, "E171", {"start": v(-14.93, 7) * mm, "end": v(-14.93, 8) * mm});
            skLineSegment(sketch, "E172", {"start": v(-14.93, 8) * mm, "end": v(-11.43, 8) * mm});
            skLineSegment(sketch, "E173", {"start": v(-0.02, 6) * mm, "end": v(0.84, 6) * mm});
            skPoint(sketch, "E174.start.orphan", {"position": v(-0.02, 6.25) * mm});
            skLineSegment(sketch, "E175", {"start": v(-0.02, 6.5) * mm, "end": v(0.84, 6.5) * mm});
            skLineSegment(sketch, "E176.trimOffspring", {"start": v(-0.02, 6) * mm, "end": v(-0.02, 5.5) * mm});
            skLineSegment(sketch, "E177.trimOffspring", {"start": v(-0.02, 6.5) * mm, "end": v(-0.02, 7) * mm});
            skLineSegment(sketch, "E178.trimOffspring", {"start": v(0.84, 6) * mm, "end": v(0.84, 2) * mm});
            skSolve(sketch);
        }
        {
            var Q0;
            Q0 = qSketchRegion(id + "F23", true);
            extrude(context, id + "F24", {"entities" : qUnion([Q0]), "operationType" : NewBodyOperationType.REMOVE, "oppositeDirection" : true, "depth" : 37.98 * mm, "offsetDistance" : 25 * mm});
        }
    });
